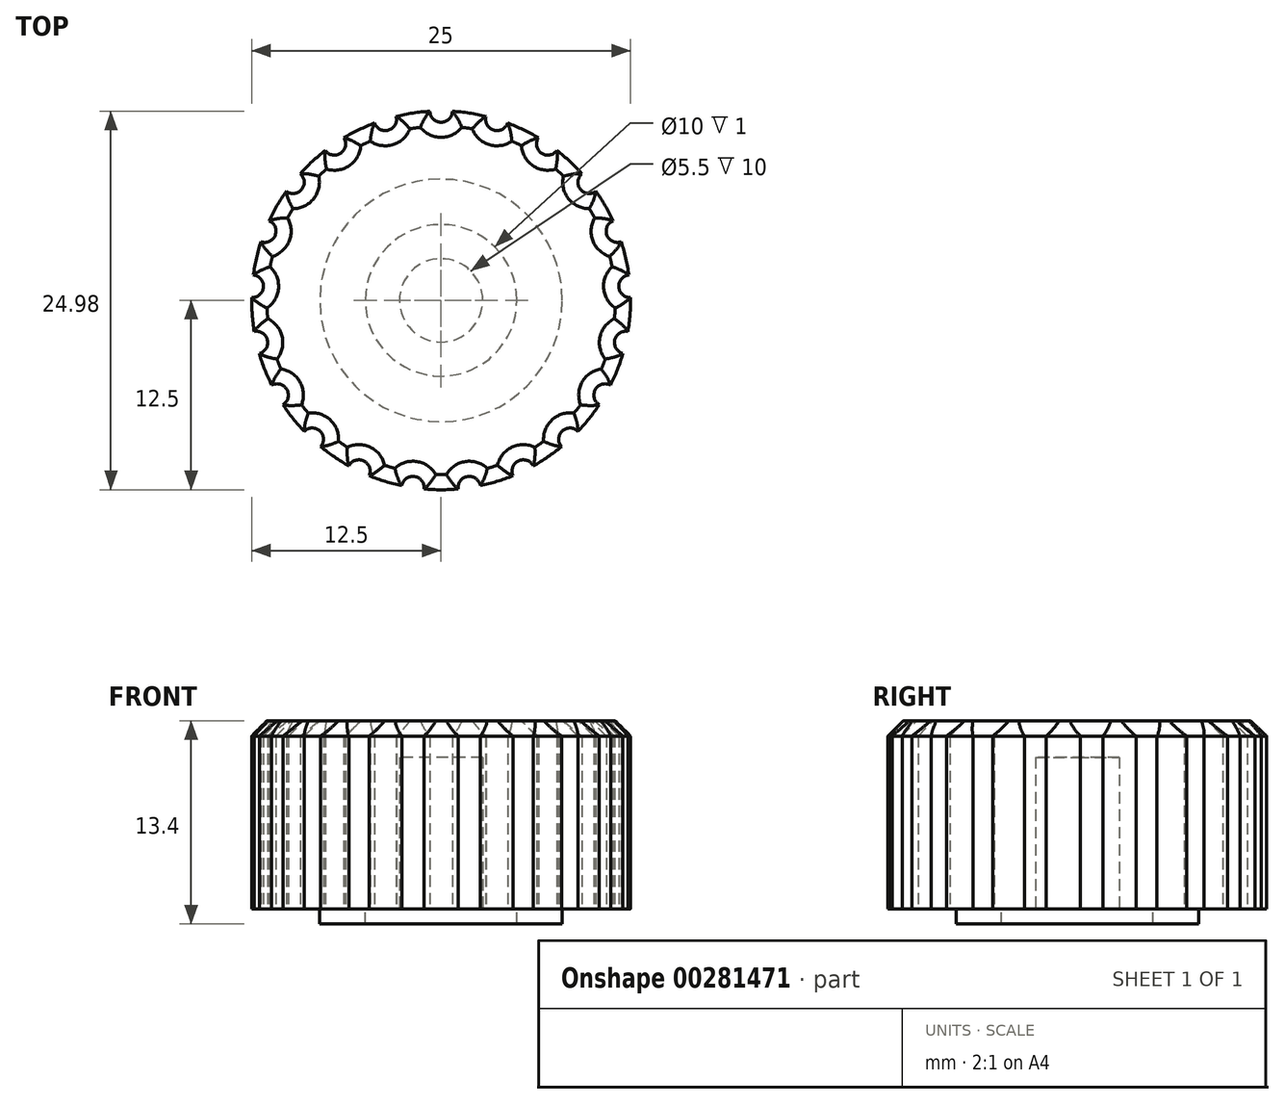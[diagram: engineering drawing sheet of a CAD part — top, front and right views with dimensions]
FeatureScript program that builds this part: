
annotation { "Feature Type Name" : "Feature", "Feature Type Description" : "" }
export const myFeature = defineFeature(function(context is Context, id is Id, definition is map)
    precondition{}
    {
        {
            var Q0;
            Q0=qCreatedBy(makeId("Top.planeOp"),FACE);
            var sketch = newSketch(context, id + "F0", { "sketchPlane" : qUnion([Q0])});
            skCircle(sketch, "E0", {"center": v(0, 0) * mm, "radius": 2.75 * mm});
            skCircle(sketch, "E1", {"center": v(0, 0) * mm, "radius": 12.5 * mm});
            skCircle(sketch, "E2", {"center": v(0, 12.5) * mm, "radius": 0.74 * mm});
            skCircle(sketch, "E3.1.0", {"center": v(-3.68, 11.94) * mm, "radius": 0.74 * mm});
            skCircle(sketch, "E3.2.0", {"center": v(-7.04, 10.33) * mm, "radius": 0.74 * mm});
            skCircle(sketch, "E3.3.0", {"center": v(-9.77, 7.8) * mm, "radius": 0.74 * mm});
            skCircle(sketch, "E3.4.0", {"center": v(-11.64, 4.57) * mm, "radius": 0.74 * mm});
            skCircle(sketch, "E3.5.0", {"center": v(-12.47, 0.93) * mm, "radius": 0.74 * mm});
            skCircle(sketch, "E3.6.0", {"center": v(-12.19, -2.78) * mm, "radius": 0.74 * mm});
            skCircle(sketch, "E3.7.0", {"center": v(-10.83, -6.25) * mm, "radius": 0.74 * mm});
            skCircle(sketch, "E3.8.0", {"center": v(-8.5, -9.16) * mm, "radius": 0.74 * mm});
            skCircle(sketch, "E3.9.0", {"center": v(-5.42, -11.26) * mm, "radius": 0.74 * mm});
            skCircle(sketch, "E3.10.0", {"center": v(-1.86, -12.36) * mm, "radius": 0.74 * mm});
            skCircle(sketch, "E3.11.0", {"center": v(1.86, -12.36) * mm, "radius": 0.74 * mm});
            skCircle(sketch, "E3.12.0", {"center": v(5.42, -11.26) * mm, "radius": 0.74 * mm});
            skCircle(sketch, "E3.13.0", {"center": v(8.5, -9.16) * mm, "radius": 0.74 * mm});
            skCircle(sketch, "E3.14.0", {"center": v(10.83, -6.25) * mm, "radius": 0.74 * mm});
            skCircle(sketch, "E3.15.0", {"center": v(12.19, -2.78) * mm, "radius": 0.74 * mm});
            skCircle(sketch, "E3.16.0", {"center": v(12.47, 0.93) * mm, "radius": 0.74 * mm});
            skCircle(sketch, "E3.17.0", {"center": v(11.64, 4.57) * mm, "radius": 0.74 * mm});
            skCircle(sketch, "E3.18.0", {"center": v(9.77, 7.8) * mm, "radius": 0.74 * mm});
            skCircle(sketch, "E3.19.0", {"center": v(7.04, 10.33) * mm, "radius": 0.74 * mm});
            skCircle(sketch, "E4.1.20.0", {"center": v(3.68, 11.94) * mm, "radius": 0.74 * mm});
            skSolve(sketch);
        }
        {
            var Q0;
            Q0=makeQuery(id+"F0.imprint","IMPRINT",FACE,{"disambiguationData":[TD([[makeQuery(id+"F0.imprint","IMPRINT",EDGE,{"derivedFrom":sQuery(id+"F0.wireOp",EDGE,"E0")}),-1.0]])]});
            extrude(context, id + "F1", {"entities" : qUnion([Q0]), "depth" : 10 * mm});
        }
        {
            var Q0;
            Q0=makeQuery(id+"F1.opExtrude","CAP_FACE",FACE,{"disambiguationData":[OSD([sQuery(id+"F0.wireOp",EDGE,"E0"),sQuery(id+"F0.wireOp",EDGE,"E1"),sQuery(id+"F0.wireOp",EDGE,"E2"),sQuery(id+"F0.wireOp",EDGE,"E3.1.0"),sQuery(id+"F0.wireOp",EDGE,"E3.2.0"),sQuery(id+"F0.wireOp",EDGE,"E3.3.0"),sQuery(id+"F0.wireOp",EDGE,"E3.4.0"),sQuery(id+"F0.wireOp",EDGE,"E3.5.0"),sQuery(id+"F0.wireOp",EDGE,"E3.6.0"),sQuery(id+"F0.wireOp",EDGE,"E3.7.0"),sQuery(id+"F0.wireOp",EDGE,"E3.8.0"),sQuery(id+"F0.wireOp",EDGE,"E3.9.0"),sQuery(id+"F0.wireOp",EDGE,"E3.10.0"),sQuery(id+"F0.wireOp",EDGE,"E3.11.0"),sQuery(id+"F0.wireOp",EDGE,"E3.12.0"),sQuery(id+"F0.wireOp",EDGE,"E3.13.0"),sQuery(id+"F0.wireOp",EDGE,"E3.14.0"),sQuery(id+"F0.wireOp",EDGE,"E3.15.0"),sQuery(id+"F0.wireOp",EDGE,"E3.16.0"),sQuery(id+"F0.wireOp",EDGE,"E3.17.0"),sQuery(id+"F0.wireOp",EDGE,"E3.18.0"),sQuery(id+"F0.wireOp",EDGE,"E3.19.0"),sQuery(id+"F0.wireOp",EDGE,"E4.1.20.0")])],"isStart":false});
            var sketch = newSketch(context, id + "F2", { "sketchPlane" : qUnion([Q0])});
            skArc(sketch, "E5.0.0", {"start": v(4.39, 11.7) * mm, "mid": v(3.47, 11.24) * mm, "end": v(2.97, 12.14) * mm});
            skArc(sketch, "E5.0.1", {"start": v(2.97, 12.14) * mm, "mid": v(1.86, 12.36) * mm, "end": v(0.74, 12.48) * mm});
            skArc(sketch, "E5.0.2", {"start": v(0.74, 12.48) * mm, "mid": v(0, 11.76) * mm, "end": v(-0.74, 12.48) * mm});
            skArc(sketch, "E5.0.3", {"start": v(-0.74, 12.48) * mm, "mid": v(-1.86, 12.36) * mm, "end": v(-2.97, 12.14) * mm});
            skArc(sketch, "E5.0.4", {"start": v(-2.97, 12.14) * mm, "mid": v(-3.47, 11.24) * mm, "end": v(-4.39, 11.7) * mm});
            skArc(sketch, "E5.0.5", {"start": v(-4.39, 11.7) * mm, "mid": v(-5.42, 11.26) * mm, "end": v(-6.42, 10.73) * mm});
            skArc(sketch, "E5.0.6", {"start": v(-6.42, 10.73) * mm, "mid": v(-6.62, 9.71) * mm, "end": v(-7.64, 9.9) * mm});
            skArc(sketch, "E5.0.7", {"start": v(-7.64, 9.9) * mm, "mid": v(-8.5, 9.16) * mm, "end": v(-9.3, 8.36) * mm});
            skArc(sketch, "E5.0.8", {"start": v(-9.3, 8.36) * mm, "mid": v(-9.2, 7.33) * mm, "end": v(-10.22, 7.2) * mm});
            skArc(sketch, "E5.0.9", {"start": v(-10.22, 7.2) * mm, "mid": v(-10.83, 6.25) * mm, "end": v(-11.34, 5.25) * mm});
            skArc(sketch, "E5.0.10", {"start": v(-11.34, 5.25) * mm, "mid": v(-10.94, 4.3) * mm, "end": v(-11.89, 3.87) * mm});
            skArc(sketch, "E5.0.11", {"start": v(-11.89, 3.87) * mm, "mid": v(-12.19, 2.78) * mm, "end": v(-12.39, 1.67) * mm});
            skArc(sketch, "E5.0.12", {"start": v(-12.39, 1.67) * mm, "mid": v(-11.72, 0.88) * mm, "end": v(-12.5, 0.2) * mm});
            skArc(sketch, "E5.0.13", {"start": v(-12.5, 0.2) * mm, "mid": v(-12.47, -0.93) * mm, "end": v(-12.33, -2.05) * mm});
            skArc(sketch, "E5.0.14", {"start": v(-12.33, -2.05) * mm, "mid": v(-11.46, -2.62) * mm, "end": v(-12, -3.5) * mm});
            skArc(sketch, "E5.0.15", {"start": v(-12, -3.5) * mm, "mid": v(-11.64, -4.57) * mm, "end": v(-11.18, -5.6) * mm});
            skArc(sketch, "E5.0.16", {"start": v(-11.18, -5.6) * mm, "mid": v(-10.18, -5.88) * mm, "end": v(-10.44, -6.88) * mm});
            skArc(sketch, "E5.0.17", {"start": v(-10.44, -6.88) * mm, "mid": v(-9.77, -7.8) * mm, "end": v(-9.03, -8.64) * mm});
            skArc(sketch, "E5.0.18", {"start": v(-9.03, -8.64) * mm, "mid": v(-8, -8.62) * mm, "end": v(-7.94, -9.65) * mm});
            skArc(sketch, "E5.0.19", {"start": v(-7.94, -9.65) * mm, "mid": v(-7.04, -10.33) * mm, "end": v(-6.08, -10.92) * mm});
            skArc(sketch, "E5.0.20", {"start": v(-6.08, -10.92) * mm, "mid": v(-5.1, -10.6) * mm, "end": v(-4.75, -11.56) * mm});
            skArc(sketch, "E5.0.21", {"start": v(-4.75, -11.56) * mm, "mid": v(-3.68, -11.94) * mm, "end": v(-2.6, -12.23) * mm});
            skArc(sketch, "E5.0.22", {"start": v(-2.6, -12.23) * mm, "mid": v(-1.75, -11.63) * mm, "end": v(-1.13, -12.45) * mm});
            skArc(sketch, "E5.0.23", {"start": v(-1.13, -12.45) * mm, "mid": v(0, -12.5) * mm, "end": v(1.13, -12.45) * mm});
            skArc(sketch, "E5.0.24", {"start": v(1.13, -12.45) * mm, "mid": v(1.75, -11.63) * mm, "end": v(2.6, -12.23) * mm});
            skArc(sketch, "E5.0.25", {"start": v(2.6, -12.23) * mm, "mid": v(3.68, -11.94) * mm, "end": v(4.75, -11.56) * mm});
            skArc(sketch, "E5.0.26", {"start": v(4.75, -11.56) * mm, "mid": v(5.1, -10.6) * mm, "end": v(6.08, -10.92) * mm});
            skArc(sketch, "E5.0.27", {"start": v(6.08, -10.92) * mm, "mid": v(7.04, -10.33) * mm, "end": v(7.94, -9.65) * mm});
            skArc(sketch, "E5.0.28", {"start": v(7.94, -9.65) * mm, "mid": v(8, -8.62) * mm, "end": v(9.03, -8.64) * mm});
            skArc(sketch, "E5.0.29", {"start": v(9.03, -8.64) * mm, "mid": v(9.77, -7.8) * mm, "end": v(10.44, -6.88) * mm});
            skArc(sketch, "E5.0.30", {"start": v(10.44, -6.88) * mm, "mid": v(10.18, -5.88) * mm, "end": v(11.18, -5.6) * mm});
            skArc(sketch, "E5.0.31", {"start": v(11.18, -5.6) * mm, "mid": v(11.64, -4.57) * mm, "end": v(12, -3.5) * mm});
            skArc(sketch, "E5.0.32", {"start": v(12, -3.5) * mm, "mid": v(11.46, -2.62) * mm, "end": v(12.33, -2.05) * mm});
            skArc(sketch, "E5.0.33", {"start": v(12.33, -2.05) * mm, "mid": v(12.47, -0.93) * mm, "end": v(12.5, 0.2) * mm});
            skArc(sketch, "E5.0.34", {"start": v(12.5, 0.2) * mm, "mid": v(11.72, 0.88) * mm, "end": v(12.39, 1.67) * mm});
            skArc(sketch, "E5.0.35", {"start": v(12.39, 1.67) * mm, "mid": v(12.19, 2.78) * mm, "end": v(11.89, 3.87) * mm});
            skArc(sketch, "E5.0.36", {"start": v(11.89, 3.87) * mm, "mid": v(10.94, 4.3) * mm, "end": v(11.34, 5.25) * mm});
            skArc(sketch, "E5.0.37", {"start": v(11.34, 5.25) * mm, "mid": v(10.83, 6.25) * mm, "end": v(10.22, 7.2) * mm});
            skArc(sketch, "E5.0.38", {"start": v(10.22, 7.2) * mm, "mid": v(9.2, 7.33) * mm, "end": v(9.3, 8.36) * mm});
            skArc(sketch, "E5.0.39", {"start": v(9.3, 8.36) * mm, "mid": v(8.5, 9.16) * mm, "end": v(7.64, 9.9) * mm});
            skArc(sketch, "E5.0.40", {"start": v(7.64, 9.9) * mm, "mid": v(6.62, 9.71) * mm, "end": v(6.42, 10.73) * mm});
            skArc(sketch, "E5.0.41", {"start": v(6.42, 10.73) * mm, "mid": v(5.42, 11.26) * mm, "end": v(4.39, 11.7) * mm});
            skSolve(sketch);
        }
        {
            var Q0;
            Q0=makeQuery(id+"F2.imprint","IMPRINT",FACE,{"disambiguationData":[TD([[makeQuery(id+"F2.imprint","IMPRINT",EDGE,{"derivedFrom":sQuery(id+"F2.wireOp",EDGE,"E5.0.0")}),-1.0]])]});
            var Q1;
            Q1=makeQuery(id+"F2.imprint","IMPRINT",FACE,{"disambiguationData":[TD([[makeQuery(id+"F2.imprint","IMPRINT",EDGE,{"derivedFrom":makeQuery(id+"F1.opExtrude","CAP_EDGE",EDGE,{"disambiguationData":[OSD([sQuery(id+"F0.wireOp",EDGE,"E0")])],"isStart":false})}),1.0]])]});
            extrude(context, id + "F3", {"entities" : qUnion([Q0, Q1]), "operationType" : NewBodyOperationType.ADD, "depth" : 2.4 * mm});
        }
        {
            var Q0;
            Q0=makeQuery(id+"F3.opExtrude","CAP_FACE",FACE,{"disambiguationData":[OSD([sQuery(id+"F2.wireOp",EDGE,"E5.0.0"),sQuery(id+"F2.wireOp",EDGE,"E5.0.1"),sQuery(id+"F2.wireOp",EDGE,"E5.0.2"),sQuery(id+"F2.wireOp",EDGE,"E5.0.3"),sQuery(id+"F2.wireOp",EDGE,"E5.0.4"),sQuery(id+"F2.wireOp",EDGE,"E5.0.5"),sQuery(id+"F2.wireOp",EDGE,"E5.0.6"),sQuery(id+"F2.wireOp",EDGE,"E5.0.7"),sQuery(id+"F2.wireOp",EDGE,"E5.0.8"),sQuery(id+"F2.wireOp",EDGE,"E5.0.9"),sQuery(id+"F2.wireOp",EDGE,"E5.0.10"),sQuery(id+"F2.wireOp",EDGE,"E5.0.11"),sQuery(id+"F2.wireOp",EDGE,"E5.0.12"),sQuery(id+"F2.wireOp",EDGE,"E5.0.13"),sQuery(id+"F2.wireOp",EDGE,"E5.0.14"),sQuery(id+"F2.wireOp",EDGE,"E5.0.15"),sQuery(id+"F2.wireOp",EDGE,"E5.0.16"),sQuery(id+"F2.wireOp",EDGE,"E5.0.17"),sQuery(id+"F2.wireOp",EDGE,"E5.0.18"),sQuery(id+"F2.wireOp",EDGE,"E5.0.19"),sQuery(id+"F2.wireOp",EDGE,"E5.0.20"),sQuery(id+"F2.wireOp",EDGE,"E5.0.21"),sQuery(id+"F2.wireOp",EDGE,"E5.0.22"),sQuery(id+"F2.wireOp",EDGE,"E5.0.23"),sQuery(id+"F2.wireOp",EDGE,"E5.0.24"),sQuery(id+"F2.wireOp",EDGE,"E5.0.25"),sQuery(id+"F2.wireOp",EDGE,"E5.0.26"),sQuery(id+"F2.wireOp",EDGE,"E5.0.27"),sQuery(id+"F2.wireOp",EDGE,"E5.0.28"),sQuery(id+"F2.wireOp",EDGE,"E5.0.29"),sQuery(id+"F2.wireOp",EDGE,"E5.0.30"),sQuery(id+"F2.wireOp",EDGE,"E5.0.31"),sQuery(id+"F2.wireOp",EDGE,"E5.0.32"),sQuery(id+"F2.wireOp",EDGE,"E5.0.33"),sQuery(id+"F2.wireOp",EDGE,"E5.0.34"),sQuery(id+"F2.wireOp",EDGE,"E5.0.35"),sQuery(id+"F2.wireOp",EDGE,"E5.0.36"),sQuery(id+"F2.wireOp",EDGE,"E5.0.37"),sQuery(id+"F2.wireOp",EDGE,"E5.0.38"),sQuery(id+"F2.wireOp",EDGE,"E5.0.39"),sQuery(id+"F2.wireOp",EDGE,"E5.0.40"),sQuery(id+"F2.wireOp",EDGE,"E5.0.41")])],"isStart":false});
            chamfer(context, id + "F4", {"entities" : qUnion([Q0]), "width" : 1 * mm, "tangentPropagation" : true});
        }
        {
            var Q0;
            Q0=makeQuery(id+"F0.imprint","IMPRINT",FACE,{"disambiguationData":[TD([[makeQuery(id+"F0.imprint","IMPRINT",EDGE,{"derivedFrom":sQuery(id+"F0.wireOp",EDGE,"E0")}),-1.0]])]});
            var sketch = newSketch(context, id + "F5", { "sketchPlane" : qUnion([Q0])});
            skCircle(sketch, "E6", {"center": v(0, 0) * mm, "radius": 5 * mm});
            skCircle(sketch, "E7.0", {"center": v(0, 0) * mm, "radius": 8 * mm});
            skSolve(sketch);
        }
        {
            var Q0;
            Q0 = qSketchRegion(id + "F5", true);
            extrude(context, id + "F6", {"entities" : qUnion([Q0]), "operationType" : NewBodyOperationType.ADD, "oppositeDirection" : true, "depth" : 1 * mm});
        }
    });
